# Revit family: 1Electronics_Community_Biamp_Subwoofer_IS6-218
name_source: partatom
category: Communication Devices
units: mm (PartAtom-declared; Revit-internal decimal feet)

## family parameters
Cut with Voids When Loaded = No
Host = Face
Maintain Annotation Orientation = No
OmniClass Number = 23.85.10.11.14.14.14
OmniClass Title = Loudspeakers
Part Type = Normal
Room Calculation Point = No
Round Connector Dimension = Use Diameter
Shared = No

## types (2) — shared parameters
Continuous Power Handling  Nominal Impedance = Single Amp - 75V, 1400W @ 4 ohms (5600W peak); Dual Amp - 75V, 700W @ 8 ohms (2800W peak) (each);
Default Elevation = 48 "
Depth = 28.89 "
Description = IS6-218 Medium Power Dual 18-Inch Subwoofer
Environmental = Outdoor: IP55W per IEC 60529, MIL-STD-810G
Equalized Maximum SPL = Half Space - Peak: 139 dB - Continuous: 133 dB; Whole Space - Peak: 133 dB - Continuous: 127 dB
Equalized Sensitivity = Half Space - 1W: 102 dB - 2.83V: 105 dB; Whole Space - 1W: 96 dB - 2.83V: 99 dB
Height = 39 "
Input Connection = Screw terminal blocks (4-position)
Manufacturer = Biamp
Mounting Points = (24) M10 threaded rigging points
Nominal Maximum SPL = Half Space - Peak: 144 dB - Continuous: 138 dB; Whole Space - Peak: 138 dB - Continuous: 132 dB
Nominal Sensitivity = Half Space - 1W: 107 dB - 2.83V: 110 dB; Whole Space - 1W: 101 dB - 2.83V: 104 dB
Operating Environment = Indoor
Operating Mode = Single or Dual Amp
Operating Range = 32 Hz to 145 Hz
Product Documentation Link = https://downloads.biamp.com
Product Page URL = https://www.biamp.com
Product data url = https://bimobject.com
Recommended Amplifiers = Single Amp - 1400W - 2800W @ 4 ohms,  (75V - 106V); Dual Amp - 700W - 1400W @ 8 ohms,  (75V - 106V) (each driver)
Shipping Weight = 190.00 lbf
Transducers = 2 x 18 (457mm) double-treated cones with 4 (102mm) inner/outer wound voice coil, ferrite construction
URL = https://www.biamp.com
Weight = 170.00 lbf
Width = 22.1 "

## per-type parameters (varying)
| type | Grill Material | Housing Material |
| IS6-218 B | Biamp - Plastic - Black(Grid) | Biamp - Plastic - Black |
| IS6-218 W | Biamp - Plastic - White(Grid) | Biamp - Plastic - White |

note: column(s) folded — value = type name in every type: Model

## geometry (parser evidence)
native form markers: Sweep x1
no freeform markers — native parametric forms only
